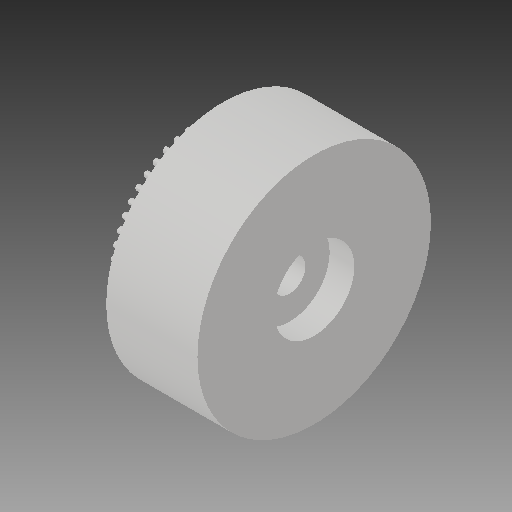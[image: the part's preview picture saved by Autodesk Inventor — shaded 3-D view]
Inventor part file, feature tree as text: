
AUTODESK INVENTOR PART (.ipt)
format: ipt  version: 2018 (Build 220112000, 112)  size: 678,912 bytes
history: native  units: in
note: dims shown in document units (in); Inventor stores cm internally (conversion verified against a paired STEP export)
features: extrude x7, sketch x7
ambient origin geometry x8: Origin, YZ Plane, XZ Plane, XY Plane, X Axis, Y Axis, Z Axis, Center Point
bodies: Solid1 (feature_tree)
feature tree (14):
  extrude  "Extrusion1"  Depth=1.0in TaperAngle=0.0deg
  extrude  "Extrusion2"  Depth=0.27in TaperAngle=0.0deg
  extrude  "Extrusion3"  Depth=0.27in TaperAngle=0.0deg
  extrude  "Extrusion7"  Depth=0.2756in TaperAngle=0.0deg
  extrude  "Extrusion8"  Depth=0.3937in TaperAngle=0.0deg
  extrude  "Extrusion9"  Depth=0.3937in TaperAngle=0.0deg
  extrude  "Extrusion10"  Depth=1.0in
  sketch  "Sketch1"  dims[d3=0.35in d4=1.0in d5=0.0in]
  sketch  "Sketch2"  dims[d6=0.865in d7=0.27in d8=0.0in]
  sketch  "Sketch3"  dims[d9=0.865in d10=0.27in d11=0.0in]
  sketch  "Sketch4"  dims[d40=18.8976in d42=360.0deg d46=0.2756in d47=0.0in]
  sketch  "Sketch5"  dims[d48=0.88in d49=0.3937in d50=0.0in]
  sketch  "Sketch7"  dims[d51=0.88in d52=0.3937in d53=0.0in]
  sketch  "Sketch8"  dims[d54=2.0in d55=2.5591in d56=2.5591in d57=1.0in d58=0.0in]
